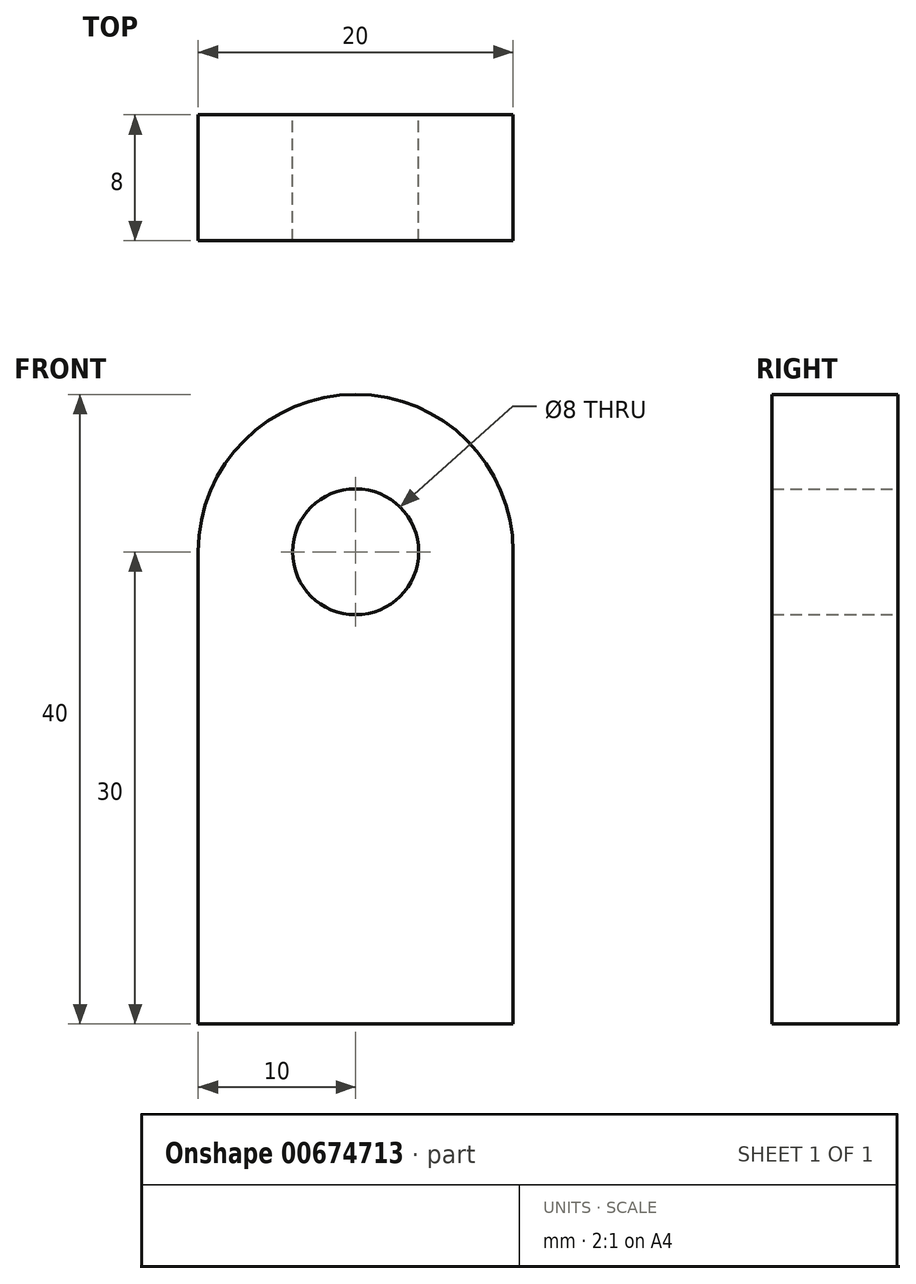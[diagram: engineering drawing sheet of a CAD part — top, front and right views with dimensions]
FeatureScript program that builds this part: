
annotation { "Feature Type Name" : "Feature", "Feature Type Description" : "" }
export const myFeature = defineFeature(function(context is Context, id is Id, definition is map)
    precondition{}
    {
        {
            var Q0;
            Q0=qCreatedBy(makeId("Front.planeOp"),FACE);
            var sketch = newSketch(context, id + "F0", { "sketchPlane" : qUnion([Q0])});
            skArc(sketch, "E0", {"start": v(10, 30) * mm, "mid": v(0, 40) * mm, "end": v(-10, 30) * mm});
            skLineSegment(sketch, "E1", {"start": v(-10, 30) * mm, "end": v(-10, 0) * mm});
            skLineSegment(sketch, "E2", {"start": v(-10, 0) * mm, "end": v(10, 0) * mm});
            skLineSegment(sketch, "E3", {"start": v(10, 0) * mm, "end": v(10, 30) * mm});
            skCircle(sketch, "E4", {"center": v(0, 30) * mm, "radius": 4 * mm});
            skSolve(sketch);
        }
        {
            var Q0;
            Q0 = qSketchRegion(id + "F0", true);
            extrude(context, id + "F1", {"entities" : qUnion([Q0]), "depth" : 8 * mm, "offsetDistance" : 25 * mm});
        }
    });
